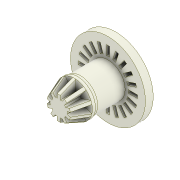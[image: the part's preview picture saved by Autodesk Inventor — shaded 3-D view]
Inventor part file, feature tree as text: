
AUTODESK INVENTOR PART (.ipt)
format: ipt  version: 2022 (Build 260153000, 153)  size: 365,568 bytes
history: native  units: mm
features: extrude x8, sketch x7, thicken_offset x2, chamfer x1, pattern_circular x1, fillet x1, plane x1, other x1
ambient origin geometry x8: Origin, YZ Plane, XZ Plane, XY Plane, X Axis, Y Axis, Z Axis, Center Point
bodies: Solid1 (feature_tree)
feature tree (22):
  extrude  "Adapter"  Depth=1.0mm TaperAngle=0.0deg
  extrude  "Motor Shaft Profile"  Depth=6.0mm
  chamfer  "Chamfer1"  Distance=12.0mm
  thicken_offset  "Thicken5"
  thicken_offset  "Thicken6"
  extrude  "Extrusion5"  Depth=2.0mm TaperAngle=45.0deg
  extrude  "Extrusion6"  Depth=0.2mm
  extrude  "Extrusion7"  Depth=1.0mm TaperAngle=0.0deg
  pattern_circular  "Circular Pattern1"  [2 undecoded]
  extrude  "Extrusion8"  Depth=1.0mm TaperAngle=0.0deg
  fillet  "Fillet1"  [1 undecoded]
  plane  "Work Plane1"
  extrude  "Extrusion9"  Depth=1.0mm TaperAngle=360.0deg
  extrude  "Extrusion10"  Depth=5.0mm
  sketch  "Sketch1"  dims[d1=11.0mm d2=1.0mm d3=0.0mm]
  sketch  "Sketch6"  dims[d4=13.0mm d5=0.0mm d35=6.0mm]
  sketch  "Sketch10"  dims[d36=5.5mm d37=12.0mm d38=0.0mm]
  sketch  "Sketch11"  dims[d39=0.2mm d40=0.1mm d48=0.5mm d49=2.0mm d50=45.0deg]
  sketch  "Sketch12"  dims[d58=0.2mm d59=0.2mm]
  sketch  "Sketch13"  dims[d74=11.5mm d75=1.0mm d76=0.0mm]
  other  "Encoder Wheel"
  sketch  "Sketch15"  dims[d77=7.5mm d78=6.0mm d79=1.0mm d80=0.0mm d81=0.0mm d82=0.0mm d83=100.0mm d84=360.0deg d86=5.0mm d87=10.0mm d88=0.0mm d89=2.0mm d90=24.0mm d91=2.5mm d92=0.0mm d93=1.0mm d94=9.5mm d95=6.5mm d96=200.0mm d98=360.0deg d100=0.0mm d101=0.0mm d102=-1.75mm d41=1.0mm d42=1.0mm d43=1.0mm d44=0.15mm d45=0.25mm d46=0.375mm d47=14.3117mm d51=0.75mm d52=0.375mm d60=0.5mm d61=0.872665mm]
note: 3 required parameter values undecoded (feature->parameter linkage not recoverable at this tier; creation-order binding heuristic only, values carry confidence <= 0.55)
